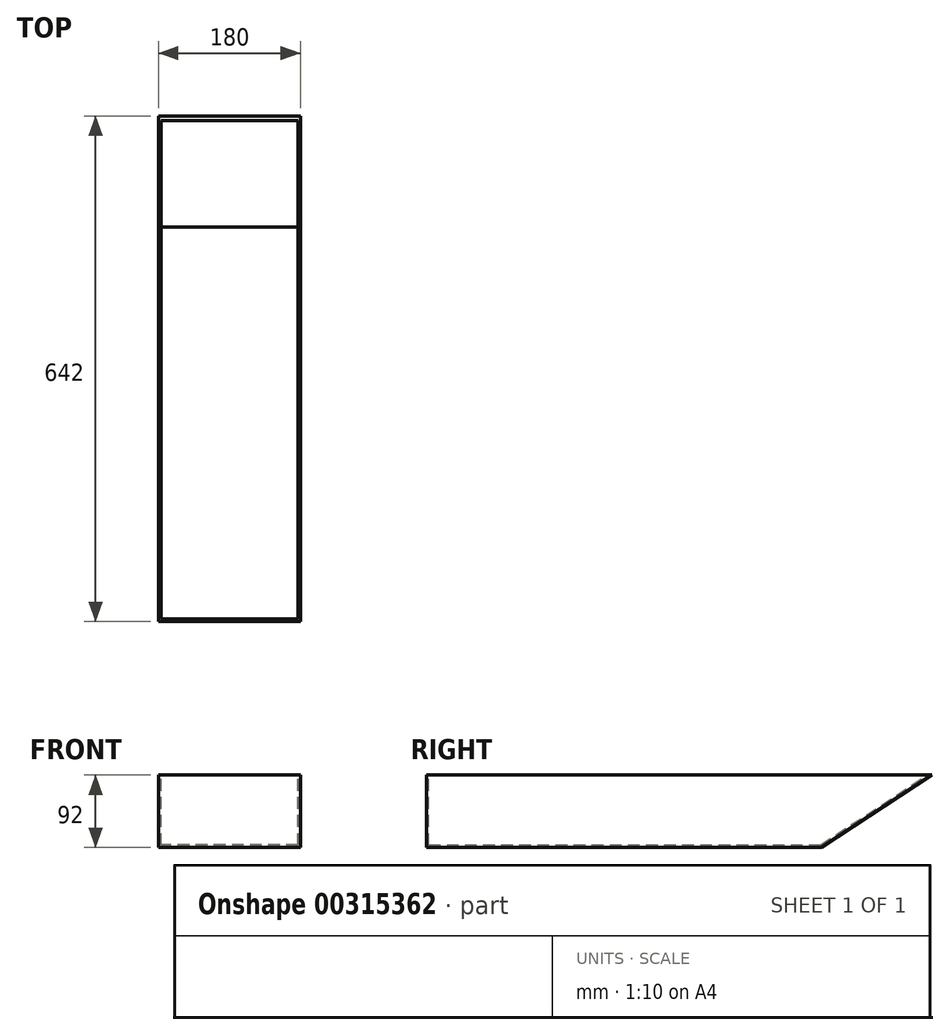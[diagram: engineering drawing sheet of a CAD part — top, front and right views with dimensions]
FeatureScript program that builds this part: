
annotation { "Feature Type Name" : "Feature", "Feature Type Description" : "" }
export const myFeature = defineFeature(function(context is Context, id is Id, definition is map)
    precondition{}
    {
        {
            var Q0;
            Q0=qCreatedBy(makeId("Right.planeOp"),FACE);
            var sketch = newSketch(context, id + "F0", { "sketchPlane" : qUnion([Q0])});
            skLineSegment(sketch, "E0.bottom", {"start": v(-251, -46) * mm, "end": v(251, -46) * mm});
            skLineSegment(sketch, "E0.top", {"start": v(-251, 46) * mm, "end": v(251, 46) * mm});
            skLineSegment(sketch, "E0.left", {"start": v(-251, -46) * mm, "end": v(-251, 46) * mm});
            skPoint(sketch, "E0.middle", {"position": v(0, 0) * mm});
            skLineSegment(sketch, "E1", {"start": v(251, -46) * mm, "end": v(391, 46) * mm});
            skLineSegment(sketch, "E2", {"start": v(391, 46) * mm, "end": v(251, 46) * mm});
            skSolve(sketch);
        }
        {
            var Q0;
            Q0 = qSketchRegion(id + "F0", true);
            extrude(context, id + "F1", {"entities" : qUnion([Q0]), "depth" : 180 * mm});
        }
        {
            var Q0;
            Q0=makeQuery(id+"F1.opExtrude","SWEPT_FACE",FACE,{"disambiguationData":[OSD([sQuery(id+"F0.wireOp",EDGE,"E0.top"),sQuery(id+"F0.wireOp",EDGE,"E2")])]});
            shell(context, id + "F2", {"entities" : qUnion([Q0]), "thickness" : 3 * mm});
        }
    });
